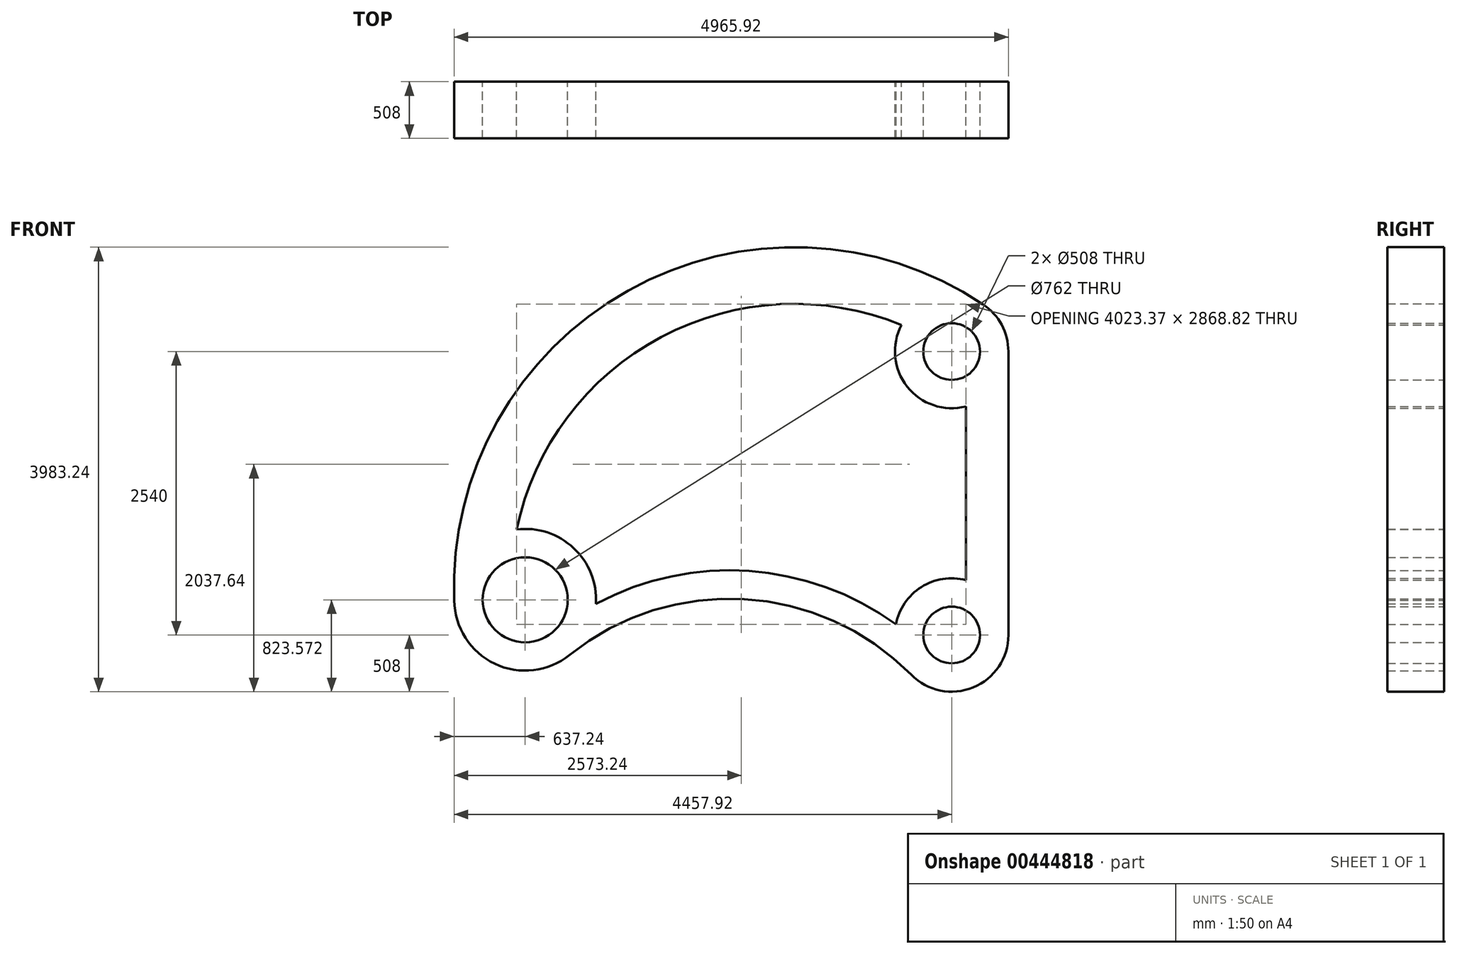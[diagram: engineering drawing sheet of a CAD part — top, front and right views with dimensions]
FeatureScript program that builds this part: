
annotation { "Feature Type Name" : "Feature", "Feature Type Description" : "" }
export const myFeature = defineFeature(function(context is Context, id is Id, definition is map)
    precondition{}
    {
        {
            var Q0;
            Q0=qCreatedBy(makeId("Front.planeOp"),FACE);
            var sketch = newSketch(context, id + "F0", { "sketchPlane" : qUnion([Q0])});
            skCircle(sketch, "E0", {"center": v(0, 2540) * mm, "radius": 254 * mm});
            skArc(sketch, "E1", {"start": v(502.33, 2464.33) * mm, "mid": v(464.59, 2745.48) * mm, "end": v(281.98, 2962.55) * mm});
            skCircle(sketch, "E2", {"center": v(0, 0) * mm, "radius": 254 * mm});
            skArc(sketch, "E3", {"start": v(127, 491.87) * mm, "mid": v(-271.9, 429.11) * mm, "end": v(-499, 95.23) * mm});
            skLineSegment(sketch, "E4", {"start": v(508, 2540) * mm, "end": v(508, 0) * mm});
            skCircle(sketch, "E5", {"center": v(-3820.68, 315.57) * mm, "radius": 381 * mm});
            skArc(sketch, "E6", {"start": v(-4455.65, 309.85) * mm, "mid": v(-4092.47, -258.32) * mm, "end": v(-3422.78, -179.3) * mm});
            skArc(sketch, "E7", {"start": v(-361.88, -356.52) * mm, "mid": v(-1858.22, 321.32) * mm, "end": v(-3422.78, -179.3) * mm});
            skArc(sketch, "E8.0", {"start": v(-448.63, 2778.31) * mm, "mid": v(-2601.9, 2670.18) * mm, "end": v(-3896.37, 946.04) * mm});
            skArc(sketch, "E9.0", {"start": v(-499, 95.23) * mm, "mid": v(-1815.87, 573.14) * mm, "end": v(-3185.82, 280.22) * mm});
            skArc(sketch, "E10.0", {"start": v(281.98, 2962.55) * mm, "mid": v(-2899.02, 3086.73) * mm, "end": v(-4455.65, 309.85) * mm});
            skLineSegment(sketch, "E11.0", {"start": v(127, 2048.13) * mm, "end": v(127, 491.87) * mm});
            skArc(sketch, "E12.trimOffspring", {"start": v(508, 2459) * mm, "mid": v(505.17, 2461.67) * mm, "end": v(502.33, 2464.33) * mm});
            skLineSegment(sketch, "E13.trimOffspring", {"start": v(-3186.74, 278.86) * mm, "end": v(-3185.82, 280.22) * mm});
            skArc(sketch, "E14.trimOffspring", {"start": v(-448.63, 2778.31) * mm, "mid": v(-398.94, 2225.5) * mm, "end": v(127, 2048.13) * mm});
            skArc(sketch, "E15.trimOffspring", {"start": v(-361.88, -356.52) * mm, "mid": v(192.65, -470.05) * mm, "end": v(508, 0) * mm});
            skArc(sketch, "E16.trimOffspring", {"start": v(-3186.74, 278.86) * mm, "mid": v(-3385.71, 778.2) * mm, "end": v(-3896.37, 946.04) * mm});
            skSolve(sketch);
        }
        {
            var Q0;
            Q0 = qSketchRegion(id + "F0", true);
            var Q1;
            Q1=makeQuery(id+"F0.imprint","IMPRINT",FACE,{"disambiguationData":[TD([[makeQuery(id+"F0.imprint","IMPRINT",EDGE,{"derivedFrom":sQuery(id+"F0.wireOp",EDGE,"E0")}),-1.0]])]});
            extrude(context, id + "F1", {"entities" : qUnion([Q0, Q1]), "depth" : 508 * mm});
        }
    });
